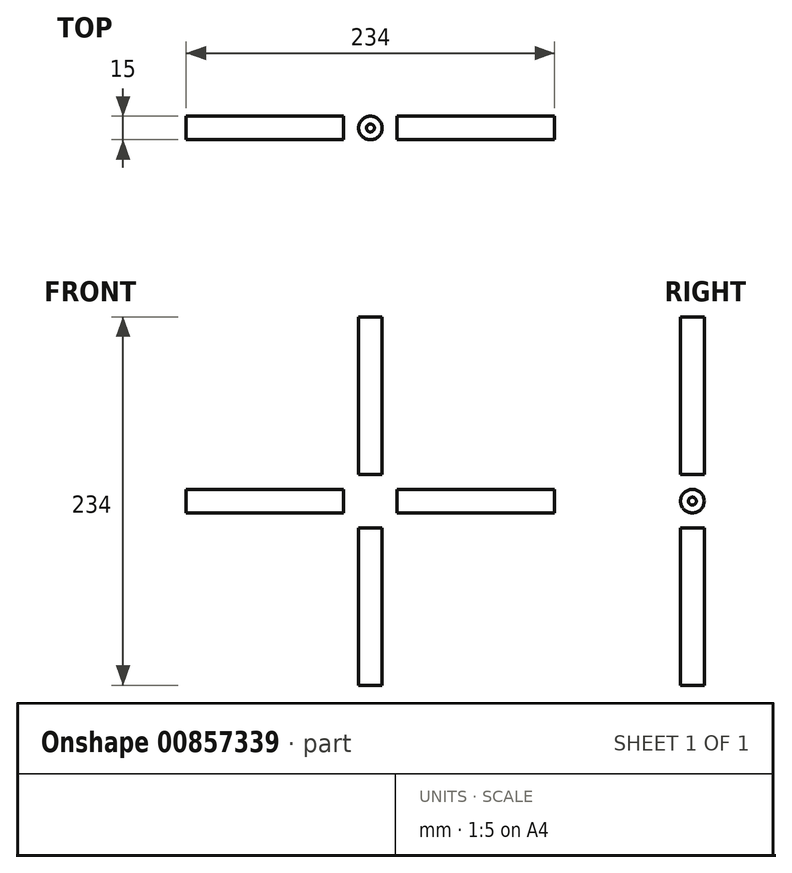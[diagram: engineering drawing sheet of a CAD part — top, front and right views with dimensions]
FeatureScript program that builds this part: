
annotation { "Feature Type Name" : "Feature", "Feature Type Description" : "" }
export const myFeature = defineFeature(function(context is Context, id is Id, definition is map)
    precondition{}
    {
        {
            var Q0;
            Q0=qCreatedBy(makeId("Front.planeOp"),FACE);
            var sketch = newSketch(context, id + "F0", { "sketchPlane" : qUnion([Q0])});
            skLineSegment(sketch, "E0", {"start": v(0, 0) * mm, "end": v(0, 17) * mm, "construction": true});
            skLineSegment(sketch, "E1.top", {"start": v(7.5, 117) * mm, "end": v(2.5, 117) * mm});
            skLineSegment(sketch, "E1.left", {"start": v(7.5, 17) * mm, "end": v(7.5, 117) * mm});
            skPoint(sketch, "E1.middle", {"position": v(0, 17) * mm});
            skLineSegment(sketch, "E2", {"start": v(7.5, 17) * mm, "end": v(2.5, 17) * mm});
            skPoint(sketch, "E1.right.end.orphan", {"position": v(-7.5, 117) * mm});
            skPoint(sketch, "E1.bottom.end.orphan", {"position": v(-7.5, -83) * mm});
            skPoint(sketch, "E3.orphan", {"position": v(7.5, -83) * mm});
            skLineSegment(sketch, "E4", {"start": v(0, 16.3) * mm, "end": v(2.5, 16.3) * mm, "construction": true});
            skLineSegment(sketch, "E5", {"start": v(2.5, 16.3) * mm, "end": v(2.5, 117) * mm});
            skPoint(sketch, "E6.start.orphan", {"position": v(0, 117) * mm});
            skLineSegment(sketch, "E7", {"start": v(0, 117) * mm, "end": v(0, 17) * mm});
            skSolve(sketch);
        }
        {
            var Q0;
            Q0=sQuery(id+"F0.wireOp",EDGE,"E2");
            var Q1;
            Q1=sQuery(id+"F0.wireOp",EDGE,"E1.top");
            var Q2;
            Q2=sQuery(id+"F0.wireOp",EDGE,"E1.left");
            var Q3;
            Q3=sQuery(id+"F0.wireOp",EDGE,"E7");
            revolve(context, id + "F1", {"bodyType" : ToolBodyType.SURFACE, "surfaceOperationType" : NewSurfaceOperationType.NEW, "surfaceEntities" : qUnion([Q0, Q1, Q2]), "axis" : qUnion([Q3]), "revolveType" : RevolveType.FULL});
        }
        {
            var Q0;
            Q0=qCreatedBy(makeId("Right.planeOp"),FACE);
            var sketch = newSketch(context, id + "F2", { "sketchPlane" : qUnion([Q0])});
            skLineSegment(sketch, "E8", {"start": v(54.7, 0) * mm, "end": v(-55.61, 0) * mm, "construction": true});
            skSolve(sketch);
        }
        {
            var Q0;
            Q0=makeQuery(id+"F1.opRevolve","SWEPT_BODY",BODY,{"disambiguationData":[OSD([sQuery(id+"F0.wireOp",EDGE,"E1.top")])]});
            var Q1;
            Q1=sQuery(id+"F2.wireOp",EDGE,"E8");
            circularPattern(context, id + "F3", {"entities" : qUnion([Q0]), "axis" : qUnion([Q1]), "angle" : 270 * degree, "instanceCount" : 4, "equalSpace" : true});
        }
    });
